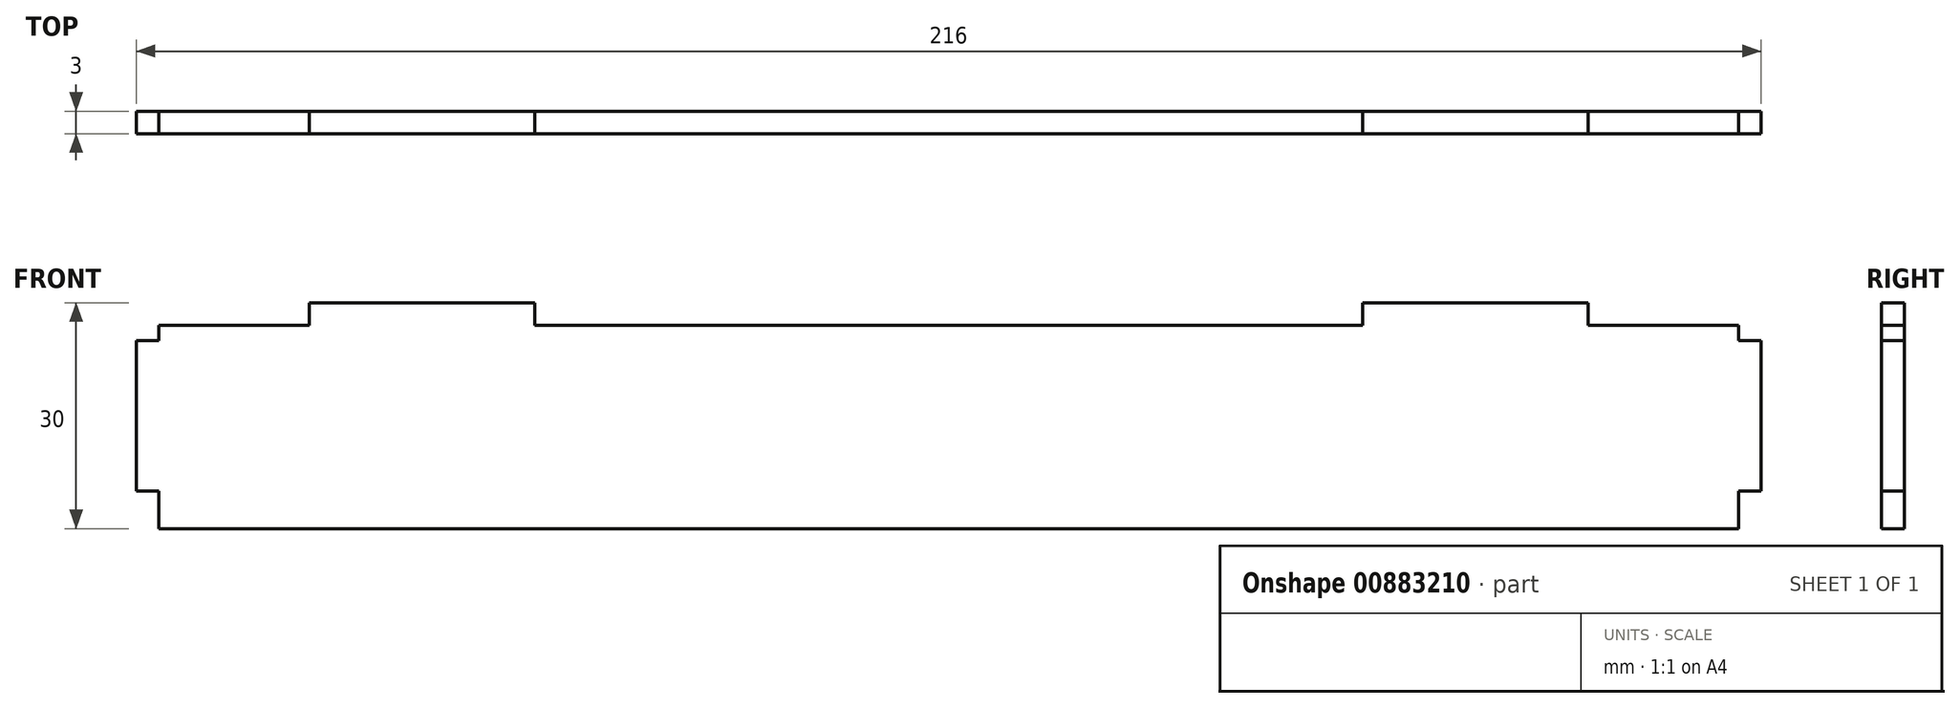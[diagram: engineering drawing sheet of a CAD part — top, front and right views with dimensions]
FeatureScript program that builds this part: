
annotation { "Feature Type Name" : "Feature", "Feature Type Description" : "" }
export const myFeature = defineFeature(function(context is Context, id is Id, definition is map)
    precondition{}
    {
        {
            var Q0;
            Q0=qCreatedBy(makeId("Front.planeOp"),FACE);
            var sketch = newSketch(context, id + "F0", { "sketchPlane" : qUnion([Q0])});
            skLineSegment(sketch, "E0.bottom", {"start": v(0, 0) * mm, "end": v(210, 0) * mm});
            skLineSegment(sketch, "E0.top", {"start": v(0, 27) * mm, "end": v(210, 27) * mm});
            skLineSegment(sketch, "E0.left", {"start": v(0, 0) * mm, "end": v(0, 27) * mm});
            skLineSegment(sketch, "E0.right", {"start": v(210, 0) * mm, "end": v(210, 27) * mm});
            skLineSegment(sketch, "E1", {"start": v(210, 25) * mm, "end": v(213, 25) * mm});
            skLineSegment(sketch, "E2", {"start": v(213, 25) * mm, "end": v(213, 5) * mm});
            skLineSegment(sketch, "E3", {"start": v(213, 5) * mm, "end": v(210, 5) * mm});
            skLineSegment(sketch, "E4", {"start": v(160, 30) * mm, "end": v(190, 30) * mm});
            skLineSegment(sketch, "E5", {"start": v(105, 27) * mm, "end": v(105, 0) * mm, "construction": true});
            skLineSegment(sketch, "E6.MirrorCS", {"start": v(50, 27) * mm, "end": v(50, 30) * mm});
            skLineSegment(sketch, "E7.MirrorCS", {"start": v(50, 30) * mm, "end": v(20, 30) * mm});
            skLineSegment(sketch, "E8.MirrorCS", {"start": v(20, 30) * mm, "end": v(20, 27) * mm});
            skLineSegment(sketch, "E9.MirrorCS", {"start": v(-3, 5) * mm, "end": v(0, 5) * mm});
            skLineSegment(sketch, "E10.MirrorCS", {"start": v(-3, 25) * mm, "end": v(-3, 5) * mm});
            skLineSegment(sketch, "E11.MirrorCS", {"start": v(0, 25) * mm, "end": v(-3, 25) * mm});
            skLineSegment(sketch, "E12", {"start": v(190, 30) * mm, "end": v(190, 27) * mm});
            skLineSegment(sketch, "E13", {"start": v(160, 30) * mm, "end": v(160, 27) * mm});
            skSolve(sketch);
        }
        {
            var Q0;
            {var subQ0=sQuery(id+"F0.wireOp",EDGE,"E9.MirrorCS");Q0=makeQuery(id+"F0.imprint","IMPRINT",FACE,{"disambiguationData":[TD([[makeQuery(id+"F0.imprint","IMPRINT",EDGE,{"derivedFrom":subQ0}),1.0]])]});}
            var Q1;
            {var subQ0=sQuery(id+"F0.wireOp",EDGE,"E1");Q1=makeQuery(id+"F0.imprint","IMPRINT",FACE,{"disambiguationData":[TD([[makeQuery(id+"F0.imprint","IMPRINT",EDGE,{"derivedFrom":subQ0}),-1.0]])]});}
            var Q2;
            {var subQ6=sQuery(id+"F0.wireOp",EDGE,"E0.top");Q2=makeQuery(id+"F0.imprint","IMPRINT",FACE,{"disambiguationData":[TD([[makeQuery(id+"F0.imprint","IMPRINT",EDGE,{"derivedFrom":subQ6}),-1.0]])]});}
            var Q3;
            {var subQ0=sQuery(id+"F0.wireOp",EDGE,"E6.MirrorCS");Q3=makeQuery(id+"F0.imprint","IMPRINT",FACE,{"disambiguationData":[TD([[makeQuery(id+"F0.imprint","IMPRINT",EDGE,{"derivedFrom":subQ0}),1.0]])]});}
            var Q4;
            Q4=makeQuery(id+"F0.imprint","IMPRINT",FACE,{"disambiguationData":[TD([[makeQuery(id+"F0.imprint","IMPRINT",EDGE,{"derivedFrom":sQuery(id+"F0.wireOp",EDGE,"E4")}),-1.0]])]});
            extrude(context, id + "F1", {"entities" : qUnion([Q0, Q1, Q2, Q3, Q4]), "depth" : 3 * mm, "offsetDistance" : 25 * mm});
        }
    });
